# Revit family: kawneer-350ir_impact-pr_tran-fr_916in_20616
name_source: partatom
category: Doors
revit_build: Autodesk Revit 2015 (Build: 20140905_0730(x64)
units: mm (PartAtom-declared; Revit-internal decimal feet)

## types (1)
- kawneer-350ir_impact-pr_tran-fr_916in_20616
    2-Color Option = no
    Air Infiltration (ASTM E 283) = < 1.20 cfm/ft2  @ 1.57 psf (300 Pa), Pairs of Doors
    Application = moderate traffic,high traffic
    Assembly Code = B2030110
    CSI Masterformat Code = 08 41 13
    Color = any
    Depth = 1 3/4"
    Description = The "350IR" medium stile heavy duty entrance offers a rugged appearance, features dual moment corner construction and designed to meet the code requirements of windborne debris protection.
    Design Load = 97.5 psf (4668 Pa)  - 9/16" laminate
127.5 psf (6105 PA) - all other glass
    Design Pressure = 65 psf (3112 Pa)  - 9/16" laminate
85 psf (4070 PA) - all other glass
    Door Corner Construction = Welded
    Door Handle Height = 37 1/2"
    Door Handle Material = Aluminum - ASTM B 221 - 6063-T6 alloy and temper
    Door Opening = 43"
    Door Panel Height = 84"
    Door Panel Material = Aluminum - ASTM B 221 - 6063-T6 alloy and temper
    Door Panel Width = 21 1/2"
    Function = Interior
    Function (Interior or Exterior) = Exterior
    Glass Capture = Captured
    Glass Installtion = outside
    Glass U-Factor = product not tested
    Glazing Thickness = 1/4"
    Height = 96"
    Hinging Types = Offset Pivot, Butt Hinge, Continuous Gear Hinge
    Keywords = Entrance, Door, Swing Door, Impact Resistent, Hurricane Resistent
    Manufacturer = Kawneer
    Manufacturer Part Number = 350 IR Entrance
    Model = 350 IR Entrance
    Overall U-Factor = product not tested
    Panel Inserts Material = Glass
    Performance standards = ASTM E 330
ASTM E 1886-97
DCBCCO PA 201-94
DCBCCO PA 202-94
DCBCCO PA 203-94
SBCCI SSTD 12-99
Kawneer Dual Moment Corner
    Product data url = https://bimobject.com
    Short Description = Medium Stile Impact Resistent Swing Door
    Sightline = 12"
    Type Comments = Medium Stile Impact Resistent Swing Door
    Type of Glazing = monolithic, insulating
    URL = http://www.kawneer.com
    Wall Closure = By host
    Water - Static (ASTM E 331) = < 1.20 cfm/ft2  @ 1.57 psf (300 Pa), Pairs of Doors
    Width = 48"

## geometry (parser evidence)
native form markers: Sweep x27
no freeform markers — native parametric forms only
